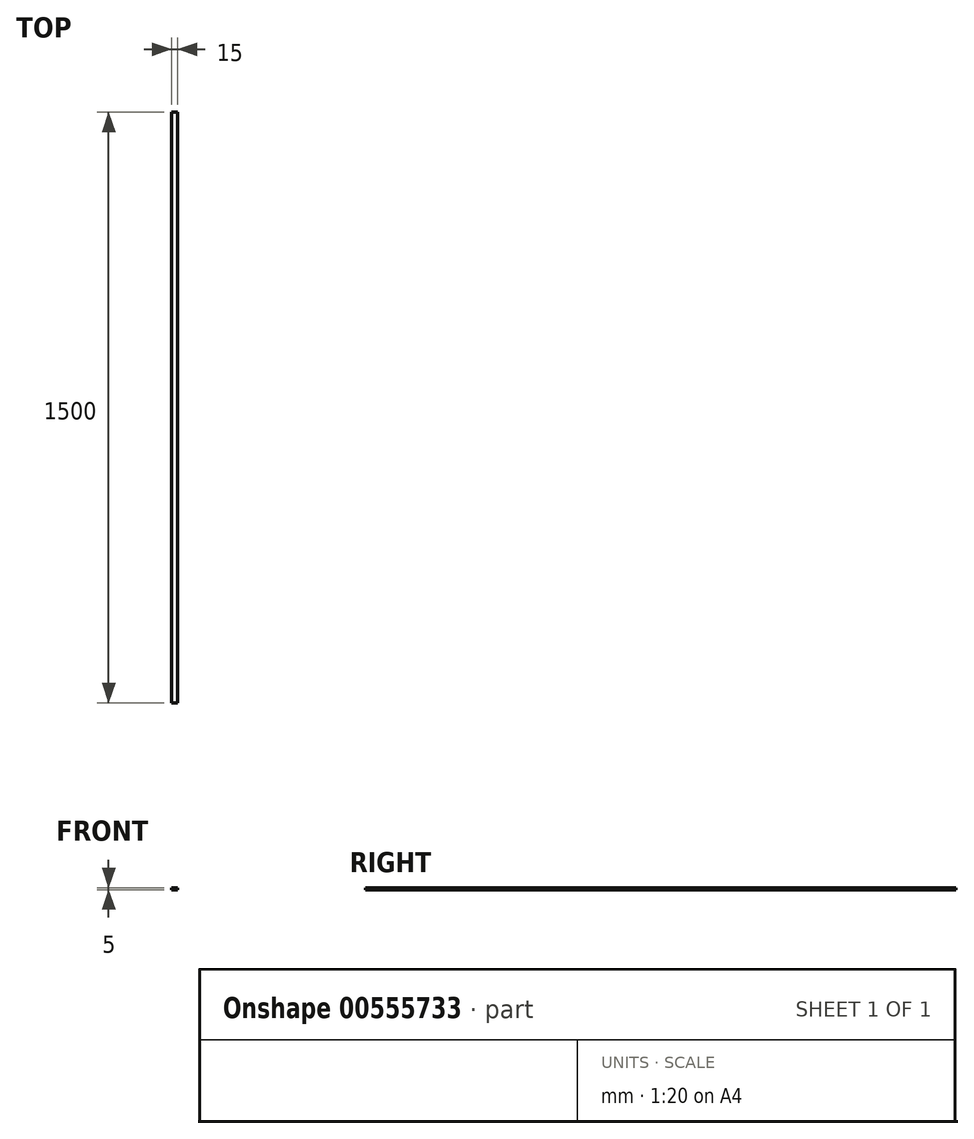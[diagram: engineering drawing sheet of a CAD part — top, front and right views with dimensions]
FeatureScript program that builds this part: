
annotation { "Feature Type Name" : "Feature", "Feature Type Description" : "" }
export const myFeature = defineFeature(function(context is Context, id is Id, definition is map)
    precondition{}
    {
        {
            var Q0;
            Q0=qCreatedBy(makeId("Top.planeOp"),FACE);
            var sketch = newSketch(context, id + "F0", { "sketchPlane" : qUnion([Q0])});
            skLineSegment(sketch, "E0.bottom", {"start": v(7.5, -750) * mm, "end": v(-7.5, -750) * mm});
            skLineSegment(sketch, "E0.top", {"start": v(7.5, 750) * mm, "end": v(-7.5, 750) * mm});
            skLineSegment(sketch, "E0.left", {"start": v(7.5, -750) * mm, "end": v(7.5, 750) * mm});
            skLineSegment(sketch, "E0.right", {"start": v(-7.5, -750) * mm, "end": v(-7.5, 750) * mm});
            skPoint(sketch, "E0.middle", {"position": v(0, 0) * mm});
            skSolve(sketch);
        }
        {
            var Q0;
            Q0=makeQuery(id+"F0.imprint","IMPRINT",FACE,{"disambiguationData":[TD([[makeQuery(id+"F0.imprint","IMPRINT",EDGE,{"derivedFrom":sQuery(id+"F0.wireOp",EDGE,"E0.bottom")}),-1.0]])]});
            extrude(context, id + "F1", {"entities" : qUnion([Q0]), "depth" : 5 * mm, "offsetDistance" : 25 * mm});
        }
    });
